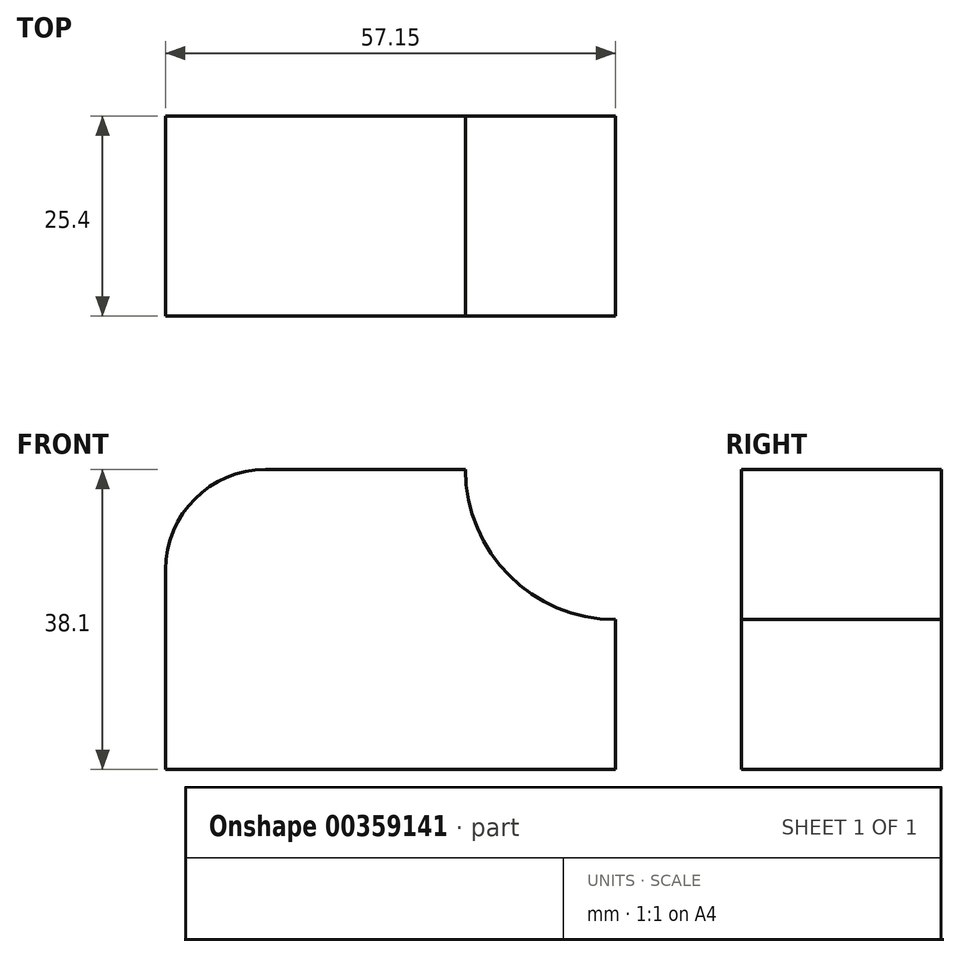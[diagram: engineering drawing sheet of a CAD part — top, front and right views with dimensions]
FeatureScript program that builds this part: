
annotation { "Feature Type Name" : "Feature", "Feature Type Description" : "" }
export const myFeature = defineFeature(function(context is Context, id is Id, definition is map)
    precondition{}
    {
        {
            var Q0;
            Q0=qCreatedBy(makeId("Front.planeOp"),FACE);
            var sketch = newSketch(context, id + "F0", { "sketchPlane" : qUnion([Q0])});
            skLineSegment(sketch, "E0.bottom", {"start": v(-19.28, 23.95) * mm, "end": v(25.17, 23.95) * mm});
            skLineSegment(sketch, "E0.top", {"start": v(-31.98, -14.15) * mm, "end": v(25.17, -14.15) * mm});
            skLineSegment(sketch, "E0.left", {"start": v(-31.98, 11.25) * mm, "end": v(-31.98, -14.15) * mm});
            skLineSegment(sketch, "E0.right", {"start": v(25.17, 23.95) * mm, "end": v(25.17, -14.15) * mm});
            skPoint(sketch, "E1.visualSharp", {"position": v(-31.98, 23.95) * mm});
            skArc(sketch, "E1.filletArc", {"start": v(-19.28, 23.95) * mm, "mid": v(-28.26, 20.23) * mm, "end": v(-31.98, 11.25) * mm});
            skLineSegment(sketch, "E2", {"start": v(6.12, 23.95) * mm, "end": v(6.12, 23.95) * mm});
            skLineSegment(sketch, "E3", {"start": v(25.17, 4.9) * mm, "end": v(25.17, 4.9) * mm});
            skPoint(sketch, "E4.visualSharp", {"position": v(6.12, 4.9) * mm});
            skArc(sketch, "E4.filletArc", {"start": v(6.12, 23.95) * mm, "mid": v(11.7, 10.48) * mm, "end": v(25.17, 4.9) * mm});
            skSolve(sketch);
        }
        {
            var Q0;
            {var subQ0=sQuery(id+"F0.wireOp",EDGE,"E0.top");Q0=makeQuery(id+"F0.imprint","IMPRINT",FACE,{"disambiguationData":[TD([[makeQuery(id+"F0.imprint","IMPRINT",EDGE,{"derivedFrom":subQ0}),1.0]])]});}
            extrude(context, id + "F1", {"entities" : qUnion([Q0]), "depth" : 25.4 * mm});
        }
    });
